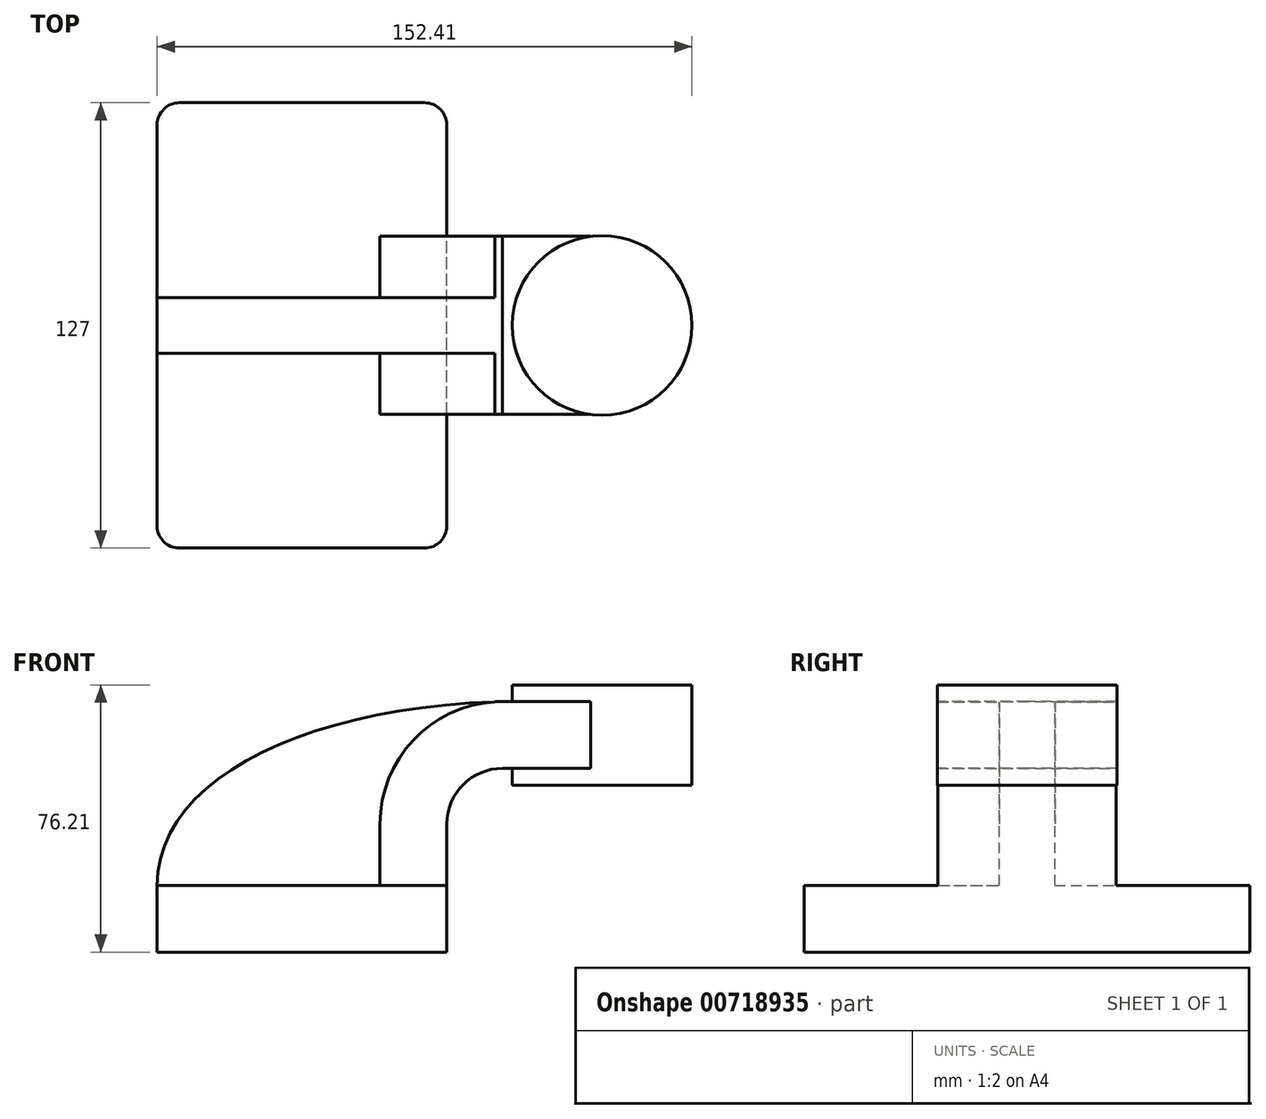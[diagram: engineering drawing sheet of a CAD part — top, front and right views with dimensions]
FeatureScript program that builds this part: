
annotation { "Feature Type Name" : "Feature", "Feature Type Description" : "" }
export const myFeature = defineFeature(function(context is Context, id is Id, definition is map)
    precondition{}
    {
        {
            var Q0;
            Q0=qCreatedBy(makeId("Front.planeOp"),FACE);
            var sketch = newSketch(context, id + "F0", { "sketchPlane" : qUnion([Q0])});
            skLineSegment(sketch, "E0.bottom", {"start": v(-41.27, -9.53) * mm, "end": v(41.28, -9.53) * mm});
            skLineSegment(sketch, "E0.top", {"start": v(-41.28, 9.53) * mm, "end": v(41.28, 9.53) * mm});
            skLineSegment(sketch, "E0.left", {"start": v(-41.28, -9.53) * mm, "end": v(-41.28, 9.53) * mm});
            skLineSegment(sketch, "E0.right", {"start": v(41.28, -9.53) * mm, "end": v(41.28, 9.53) * mm});
            skPoint(sketch, "E0.middle", {"position": v(0, 0) * mm});
            skLineSegment(sketch, "E1.bottom", {"start": v(60.32, 38.1) * mm, "end": v(111.12, 38.1) * mm});
            skLineSegment(sketch, "E1.top", {"start": v(60.32, 66.67) * mm, "end": v(111.12, 66.67) * mm});
            skLineSegment(sketch, "E1.left", {"start": v(60.32, 38.1) * mm, "end": v(60.32, 66.67) * mm});
            skLineSegment(sketch, "E1.right", {"start": v(111.12, 38.1) * mm, "end": v(111.12, 66.67) * mm});
            skPoint(sketch, "E1.middle", {"position": v(85.72, 52.39) * mm});
            skLineSegment(sketch, "E2", {"start": v(41.27, 9.52) * mm, "end": v(41.27, 27) * mm});
            skArc(sketch, "E3", {"start": v(41.27, 27) * mm, "mid": v(45.92, 38.23) * mm, "end": v(57.15, 42.88) * mm});
            skLineSegment(sketch, "E4", {"start": v(57.15, 42.88) * mm, "end": v(85.51, 42.88) * mm});
            skLineSegment(sketch, "E5.0", {"start": v(57.15, 61.93) * mm, "end": v(85.51, 61.93) * mm});
            skArc(sketch, "E5.1", {"start": v(22.22, 27) * mm, "mid": v(32.45, 51.7) * mm, "end": v(57.15, 61.93) * mm});
            skLineSegment(sketch, "E5.2", {"start": v(22.22, 9.52) * mm, "end": v(22.22, 27) * mm});
            skLineSegment(sketch, "E6", {"start": v(85.51, 38.1) * mm, "end": v(85.51, 66.67) * mm});
            skFitSpline(sketch, "E7", {"points": [v(-41.27, 9.53) * mm, v(57.15, 61.93) * mm], "startDerivative": vector(0.34, 91.73) * mm, "endDerivative": vector(167.53, 4.55) * mm});
            skSolve(sketch);
        }
        {
            var Q0;
            Q0=makeQuery(id+"F0.imprint","IMPRINT",FACE,{"disambiguationData":[TD([[makeQuery(id+"F0.imprint","IMPRINT",EDGE,{"derivedFrom":sQuery(id+"F0.wireOp",EDGE,"E0.bottom")}),1.0]])]});
            var Q1;
            Q1=sQuery(id+"F0.wireOp",EDGE,"E7");
            extrude(context, id + "F1", {"entities" : qUnion([Q0]), "surfaceEntities" : qUnion([Q1]), "endBound" : BoundingType.SYMMETRIC, "depth" : 127 * mm, "offsetDistance" : 25.4 * mm});
        }
        {
            var Q0;
            {var subQ1=sQuery(id+"F0.wireOp",EDGE,"E2");Q0=makeQuery(id+"F0.imprint","IMPRINT",FACE,{"disambiguationData":[TD([[makeQuery(id+"F0.imprint","IMPRINT",EDGE,{"derivedFrom":subQ1}),1.0]])]});}
            var Q1;
            {var subQ0=sQuery(id+"F0.wireOp",EDGE,"E4");var subQ1=sQuery(id+"F0.wireOp",EDGE,"E1.left");var subQ2=makeQuery(id+"F0.imprint","INTERSECT",VERTEX,{"derivedFrom":[subQ1,subQ0]});Q1=makeQuery(id+"F0.imprint","IMPRINT",FACE,{"disambiguationData":[TD([[makeQuery(id+"F0.imprint","IMPRINT",EDGE,{"disambiguationData":[TD([[subQ2,-1.0]])],"derivedFrom":subQ1}),-1.0]])]});}
            extrude(context, id + "F2", {"entities" : qUnion([Q0, Q1]), "operationType" : NewBodyOperationType.ADD, "endBound" : BoundingType.SYMMETRIC, "depth" : 50.8 * mm, "offsetDistance" : 25.4 * mm});
        }
        {
            var Q0;
            {var subQ3=sQuery(id+"F0.wireOp",EDGE,"E5.2");Q0=makeQuery(id+"F0.imprint","IMPRINT",FACE,{"disambiguationData":[TD([[makeQuery(id+"F0.imprint","IMPRINT",EDGE,{"derivedFrom":subQ3}),1.0]])]});}
            extrude(context, id + "F3", {"entities" : qUnion([Q0]), "operationType" : NewBodyOperationType.ADD, "endBound" : BoundingType.SYMMETRIC, "depth" : 15.88 * mm, "offsetDistance" : 25.4 * mm});
        }
        {
            var Q0;
            {var subQ4=sQuery(id+"F0.wireOp",EDGE,"E1.right");Q0=makeQuery(id+"F0.imprint","IMPRINT",FACE,{"disambiguationData":[TD([[makeQuery(id+"F0.imprint","IMPRINT",EDGE,{"derivedFrom":subQ4}),1.0]])]});}
            var Q1;
            Q1=sQuery(id+"F0.wireOp",EDGE,"E6");
            revolve(context, id + "F4", {"operationType" : NewBodyOperationType.ADD, "surfaceOperationType" : NewSurfaceOperationType.NEW, "entities" : qUnion([Q0]), "axis" : qUnion([Q1]), "revolveType" : RevolveType.FULL});
        }
        {
            var Q0;
            Q0=makeQuery(id+"F1.opExtrude","CAP_EDGE",EDGE,{"disambiguationData":[OSD([sQuery(id+"F0.wireOp",EDGE,"E0.right")])],"isStart":false});
            var Q1;
            Q1=makeQuery(id+"F1.opExtrude","CAP_EDGE",EDGE,{"disambiguationData":[OSD([sQuery(id+"F0.wireOp",EDGE,"E0.left")])],"isStart":false});
            var Q2;
            Q2=makeQuery(id+"F1.opExtrude","CAP_EDGE",EDGE,{"disambiguationData":[OSD([sQuery(id+"F0.wireOp",EDGE,"E0.right")])],"isStart":true});
            var Q3;
            Q3=makeQuery(id+"F1.opExtrude","CAP_EDGE",EDGE,{"disambiguationData":[OSD([sQuery(id+"F0.wireOp",EDGE,"E0.left")])],"isStart":true});
            fillet(context, id + "F5", {"entities" : qUnion([Q0, Q1, Q2, Q3]), "radius" : 6.35 * mm, "tangentPropagation" : true, "allowEdgeOverflow" : false});
        }
    });
